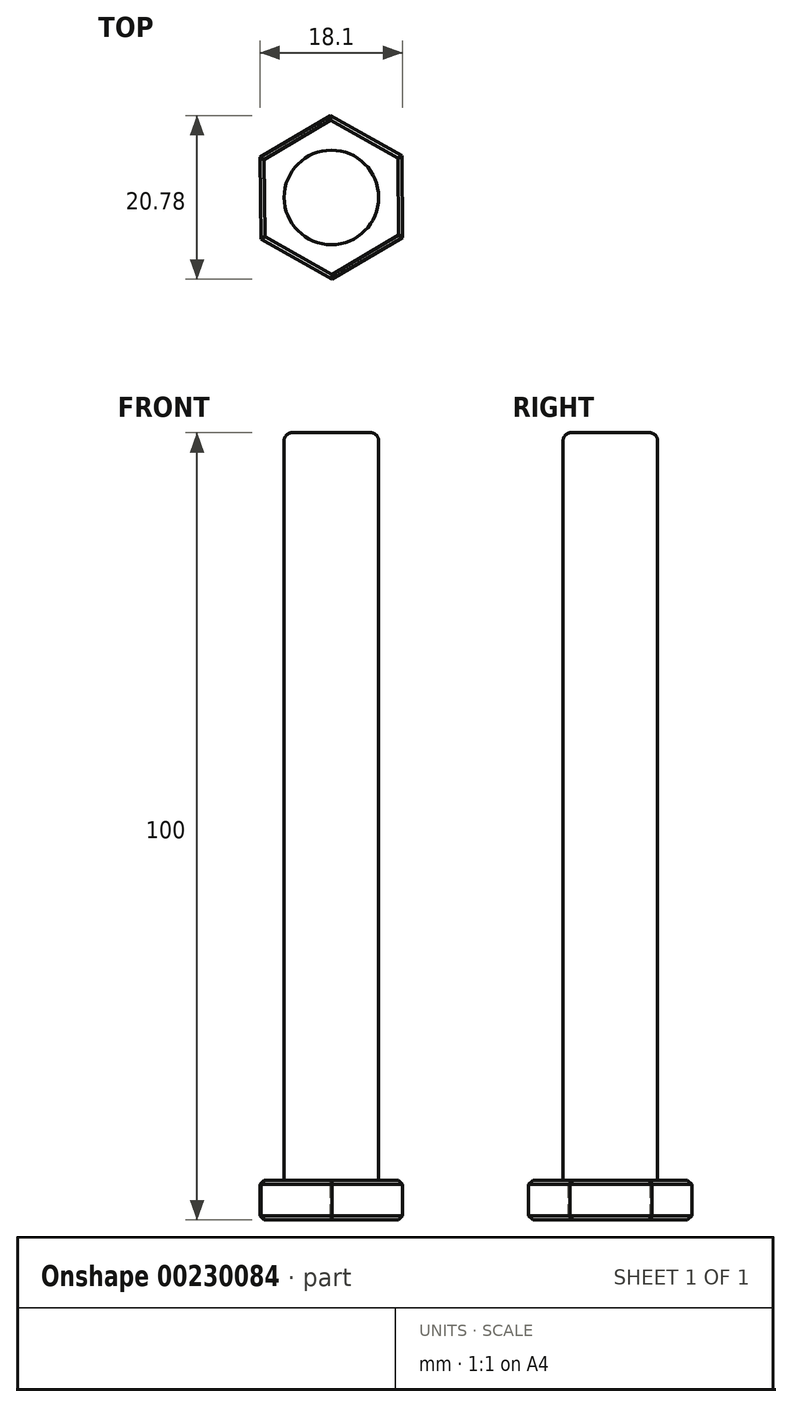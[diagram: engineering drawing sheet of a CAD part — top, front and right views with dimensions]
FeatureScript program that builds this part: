
annotation { "Feature Type Name" : "Feature", "Feature Type Description" : "" }
export const myFeature = defineFeature(function(context is Context, id is Id, definition is map)
    precondition{}
    {
        {
            var Q0;
            Q0=qCreatedBy(makeId("Top.planeOp"),FACE);
            var sketch = newSketch(context, id + "F0", { "sketchPlane" : qUnion([Q0])});
            skCircle(sketch, "E0.cCircle", {"center": v(0, 0) * mm, "radius": 9 * mm, "construction": true});
            skLineSegment(sketch, "E0.0", {"start": v(-0.1, 10.4) * mm, "end": v(8.95, 5.29) * mm});
            skLineSegment(sketch, "E0.1", {"start": v(8.95, 5.29) * mm, "end": v(9.05, -5.1) * mm});
            skLineSegment(sketch, "E0.2", {"start": v(9.05, -5.1) * mm, "end": v(0.1, -10.4) * mm});
            skLineSegment(sketch, "E0.3", {"start": v(0.1, -10.4) * mm, "end": v(-8.95, -5.29) * mm});
            skLineSegment(sketch, "E0.4", {"start": v(-8.95, -5.29) * mm, "end": v(-9.05, 5.1) * mm});
            skLineSegment(sketch, "E0.5", {"start": v(-9.05, 5.1) * mm, "end": v(-0.1, 10.4) * mm});
            skPoint(sketch, "E0.0.midPoint", {"position": v(4.42, 7.84) * mm});
            skCircle(sketch, "E1", {"center": v(0, 0) * mm, "radius": 6 * mm});
            skSolve(sketch);
        }
        {
            var Q0;
            Q0=makeQuery(id+"F0.imprint","IMPRINT",FACE,{"disambiguationData":[TD([[makeQuery(id+"F0.imprint","IMPRINT",EDGE,{"derivedFrom":sQuery(id+"F0.wireOp",EDGE,"E1")}),1.0]])]});
            extrude(context, id + "F1", {"entities" : qUnion([Q0]), "depth" : 95 * mm});
        }
        {
            var Q0;
            Q0 = qSketchRegion(id + "F0", true);
            var Q1;
            Q1=makeQuery(id+"F1.opExtrude","CAP_FACE",FACE,{"disambiguationData":[OSD([sQuery(id+"F0.wireOp",EDGE,"E1")])],"isStart":true});
            extrude(context, id + "F2", {"entities" : qUnion([Q0, Q1]), "operationType" : NewBodyOperationType.ADD, "oppositeDirection" : true, "depth" : 5 * mm});
        }
        {
            var Q0;
            Q0=makeQuery(id+"F1.opExtrude","CAP_EDGE",EDGE,{"disambiguationData":[OSD([sQuery(id+"F0.wireOp",EDGE,"E1")])],"isStart":false});
            fillet(context, id + "F3", {"entities" : qUnion([Q0]), "radius" : 1 * mm, "tangentPropagation" : true, "allowEdgeOverflow" : false});
        }
        {
            var Q0;
            Q0=makeQuery(id+"F2.opExtrude","CAP_EDGE",EDGE,{"disambiguationData":[OSD([sQuery(id+"F0.wireOp",EDGE,"E0.0")])],"isStart":false});
            var Q1;
            Q1=makeQuery(id+"F2.opExtrude","CAP_EDGE",EDGE,{"disambiguationData":[OSD([sQuery(id+"F0.wireOp",EDGE,"E0.5")])],"isStart":false});
            var Q2;
            Q2=makeQuery(id+"F2.opExtrude","CAP_EDGE",EDGE,{"disambiguationData":[OSD([sQuery(id+"F0.wireOp",EDGE,"E0.4")])],"isStart":false});
            var Q3;
            Q3=makeQuery(id+"F2.opExtrude","CAP_EDGE",EDGE,{"disambiguationData":[OSD([sQuery(id+"F0.wireOp",EDGE,"E0.3")])],"isStart":false});
            var Q4;
            Q4=makeQuery(id+"F2.opExtrude","CAP_EDGE",EDGE,{"disambiguationData":[OSD([sQuery(id+"F0.wireOp",EDGE,"E0.2")])],"isStart":false});
            var Q5;
            Q5=makeQuery(id+"F2.opExtrude","CAP_EDGE",EDGE,{"disambiguationData":[OSD([sQuery(id+"F0.wireOp",EDGE,"E0.1")])],"isStart":false});
            var Q6;
            Q6=makeQuery(id+"F2.opExtrude","CAP_EDGE",EDGE,{"disambiguationData":[OSD([sQuery(id+"F0.wireOp",EDGE,"E0.5")])],"isStart":true});
            var Q7;
            Q7=makeQuery(id+"F2.opExtrude","CAP_EDGE",EDGE,{"disambiguationData":[OSD([sQuery(id+"F0.wireOp",EDGE,"E0.4")])],"isStart":true});
            var Q8;
            Q8=makeQuery(id+"F2.opExtrude","CAP_EDGE",EDGE,{"disambiguationData":[OSD([sQuery(id+"F0.wireOp",EDGE,"E0.3")])],"isStart":true});
            var Q9;
            Q9=makeQuery(id+"F2.opExtrude","CAP_EDGE",EDGE,{"disambiguationData":[OSD([sQuery(id+"F0.wireOp",EDGE,"E0.2")])],"isStart":true});
            var Q10;
            Q10=makeQuery(id+"F2.opExtrude","CAP_EDGE",EDGE,{"disambiguationData":[OSD([sQuery(id+"F0.wireOp",EDGE,"E0.0")])],"isStart":true});
            var Q11;
            Q11=makeQuery(id+"F2.opExtrude","CAP_EDGE",EDGE,{"disambiguationData":[OSD([sQuery(id+"F0.wireOp",EDGE,"E0.1")])],"isStart":true});
            chamfer(context, id + "F4", {"entities" : qUnion([Q0, Q1, Q2, Q3, Q4, Q5, Q6, Q7, Q8, Q9, Q10, Q11]), "width" : 0.5 * mm, "tangentPropagation" : true});
        }
    });
